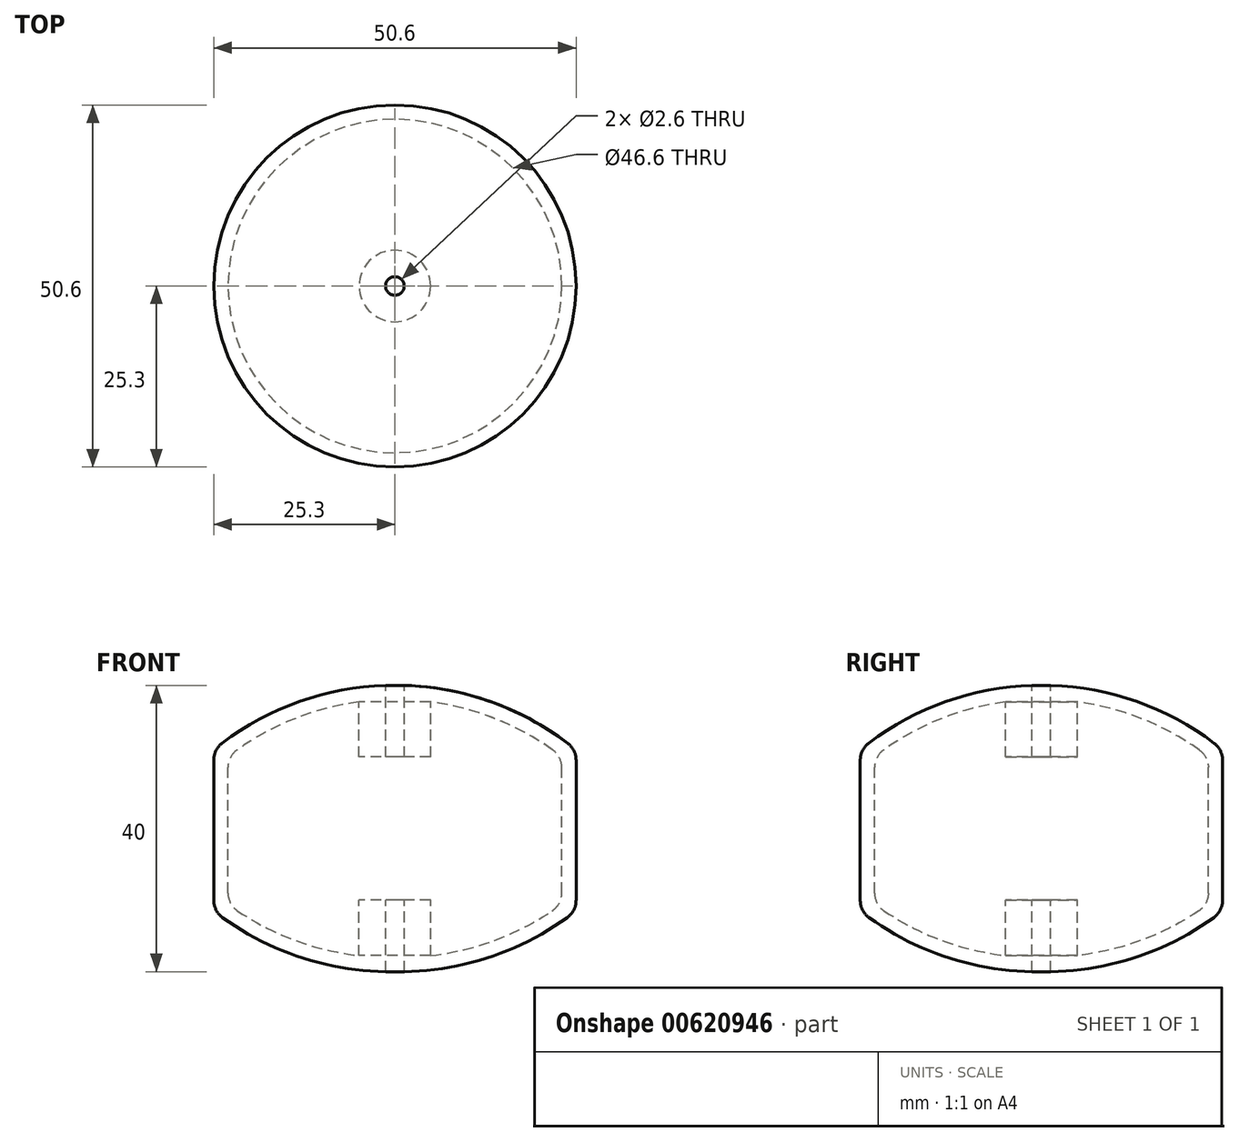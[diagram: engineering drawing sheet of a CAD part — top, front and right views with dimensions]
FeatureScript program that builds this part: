
annotation { "Feature Type Name" : "Feature", "Feature Type Description" : "" }
export const myFeature = defineFeature(function(context is Context, id is Id, definition is map)
    precondition{}
    {
        {
            var Q0;
            Q0=qCreatedBy(makeId("Front.planeOp"),FACE);
            var sketch = newSketch(context, id + "F0", { "sketchPlane" : qUnion([Q0])});
            skLineSegment(sketch, "E0.bottom", {"start": v(5, 0) * mm, "end": v(1.3, 0) * mm});
            skLineSegment(sketch, "E0.left", {"start": v(5, 0) * mm, "end": v(5, 7.7) * mm});
            skLineSegment(sketch, "E1", {"start": v(0, 0) * mm, "end": v(0, -6) * mm});
            skLineSegment(sketch, "E2", {"start": v(1.3, 10) * mm, "end": v(1.3, 0) * mm});
            skArc(sketch, "E3", {"start": v(1.3, 10) * mm, "mid": v(13.33, 7.74) * mm, "end": v(24.1, 1.94) * mm});
            skArc(sketch, "E4", {"start": v(5, 7.7) * mm, "mid": v(13.93, 5.38) * mm, "end": v(22.04, 0.98) * mm});
            skLineSegment(sketch, "E5", {"start": v(1.3, -30) * mm, "end": v(1.3, -20) * mm});
            skLineSegment(sketch, "E6", {"start": v(1.3, -20) * mm, "end": v(5, -20) * mm});
            skLineSegment(sketch, "E7", {"start": v(5, -20) * mm, "end": v(5, -27.75) * mm});
            skArc(sketch, "E8.trimOffspring", {"start": v(24.05, -22.45) * mm, "mid": v(13.26, -27.97) * mm, "end": v(1.3, -30) * mm});
            skLineSegment(sketch, "E9", {"start": v(25.3, -0.45) * mm, "end": v(25.3, -20.01) * mm});
            skLineSegment(sketch, "E10", {"start": v(23.3, -1.47) * mm, "end": v(23.3, -19.01) * mm});
            skArc(sketch, "E11.trimOffspring", {"start": v(21.98, -21.5) * mm, "mid": v(13.87, -25.65) * mm, "end": v(5, -27.75) * mm});
            skPoint(sketch, "E12.orphan", {"position": v(35.3, -10) * mm});
            skPoint(sketch, "E13.trimOffspring.end.orphan", {"position": v(32.32, -10) * mm});
            skPoint(sketch, "E14.orphan", {"position": v(34.65, -10) * mm});
            skPoint(sketch, "E15.visualSharp", {"position": v(23.3, 0.04) * mm});
            skArc(sketch, "E15.filletArc", {"start": v(23.3, -1.47) * mm, "mid": v(22.97, -0.1) * mm, "end": v(22.04, 0.98) * mm});
            skPoint(sketch, "E16.visualSharp", {"position": v(23.3, -20.56) * mm});
            skArc(sketch, "E16.filletArc", {"start": v(21.98, -21.5) * mm, "mid": v(22.95, -20.42) * mm, "end": v(23.3, -19.01) * mm});
            skPoint(sketch, "E17.visualSharp", {"position": v(25.3, 1) * mm});
            skArc(sketch, "E17.filletArc", {"start": v(25.3, -0.45) * mm, "mid": v(24.99, 0.88) * mm, "end": v(24.1, 1.94) * mm});
            skPoint(sketch, "E18.visualSharp", {"position": v(25.3, -21.51) * mm});
            skArc(sketch, "E18.filletArc", {"start": v(24.05, -22.45) * mm, "mid": v(24.97, -21.38) * mm, "end": v(25.3, -20.01) * mm});
            skSolve(sketch);
        }
        {
            var Q0;
            Q0 = qSketchRegion(id + "F0", true);
            var Q1;
            Q1=sQuery(id+"F0.wireOp",EDGE,"E1");
            revolve(context, id + "F1", {"entities" : qUnion([Q0]), "axis" : qUnion([Q1]), "revolveType" : RevolveType.FULL});
        }
    });
